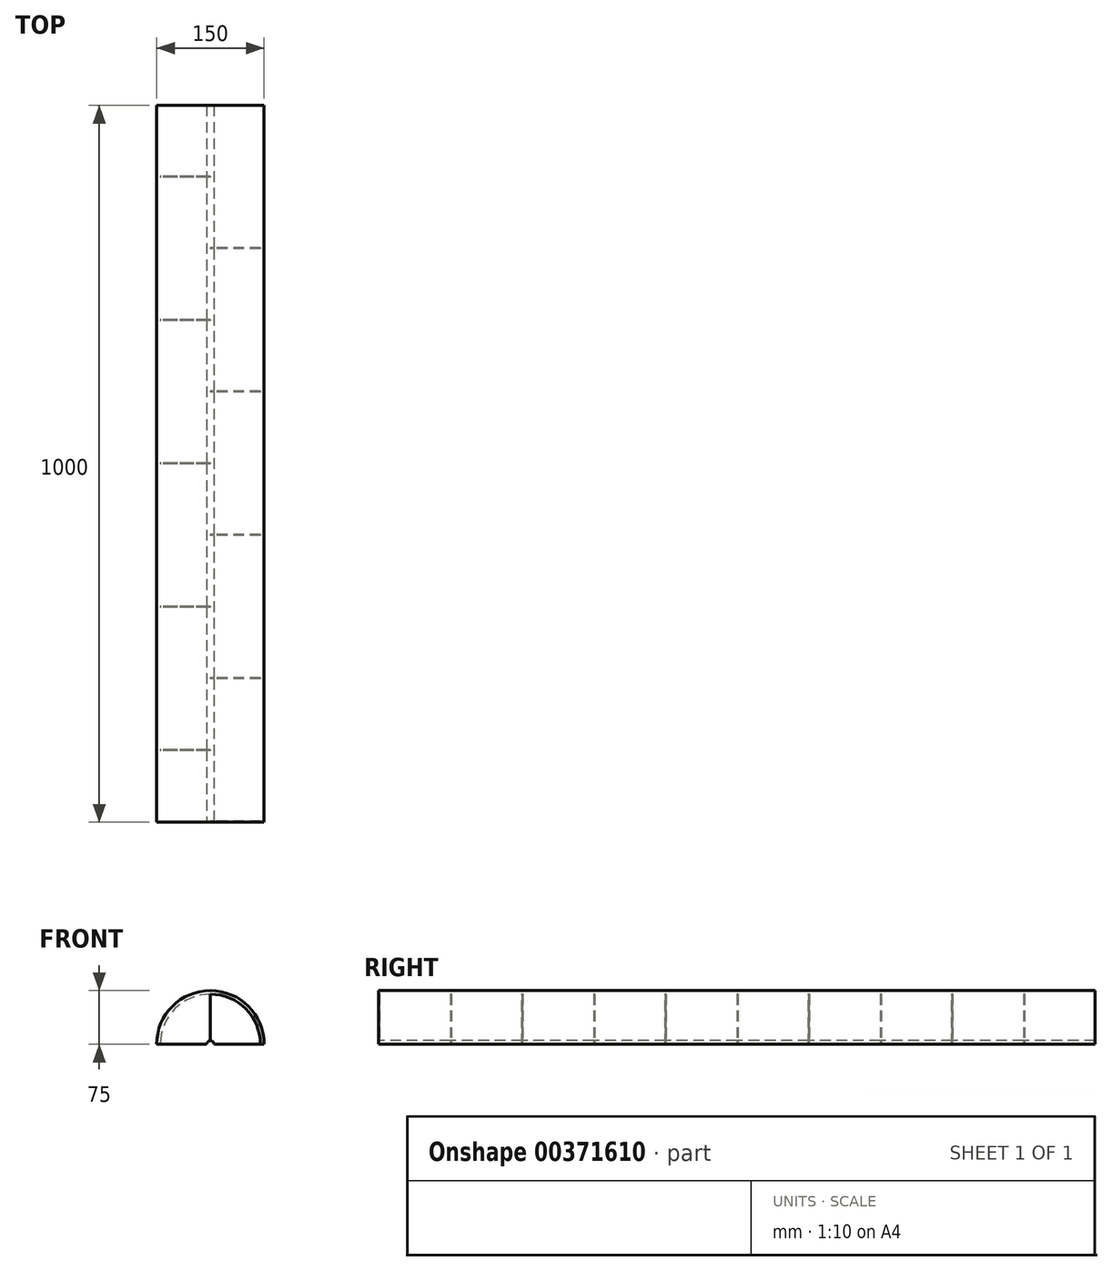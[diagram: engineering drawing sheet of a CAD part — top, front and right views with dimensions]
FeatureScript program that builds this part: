
annotation { "Feature Type Name" : "Feature", "Feature Type Description" : "" }
export const myFeature = defineFeature(function(context is Context, id is Id, definition is map)
    precondition{}
    {
        {
            var Q0;
            Q0=qCreatedBy(makeId("Front.planeOp"),FACE);
            var sketch = newSketch(context, id + "F0", { "sketchPlane" : qUnion([Q0])});
            skCircle(sketch, "E0", {"center": v(0, 0) * mm, "radius": 75 * mm});
            skSolve(sketch);
        }
        {
            var Q0;
            Q0 = qSketchRegion(id + "F0", true);
            extrude(context, id + "F1", {"entities" : qUnion([Q0]), "oppositeDirection" : true, "depth" : 1000 * mm});
        }
        {
            var Q0;
            Q0=qCreatedBy(makeId("Front.planeOp"),FACE);
            var sketch = newSketch(context, id + "F2", { "sketchPlane" : qUnion([Q0])});
            skCircle(sketch, "E1", {"center": v(0, 0) * mm, "radius": 5 * mm});
            skSolve(sketch);
        }
        {
            var Q0;
            Q0 = qSketchRegion(id + "F2", true);
            extrude(context, id + "F3", {"entities" : qUnion([Q0]), "operationType" : NewBodyOperationType.REMOVE, "oppositeDirection" : true, "depth" : 1000 * mm});
        }
        {
            var Q0;
            Q0=qCreatedBy(makeId("Front.planeOp"),FACE);
            var sketch = newSketch(context, id + "F4", { "sketchPlane" : qUnion([Q0])});
            skArc(sketch, "E2", {"start": v(0, -70) * mm, "mid": v(70, 0) * mm, "end": v(0, 70) * mm});
            skLineSegment(sketch, "E3", {"start": v(0, 70) * mm, "end": v(0, -70) * mm});
            skSolve(sketch);
        }
        {
            var Q0;
            Q0 = qSketchRegion(id + "F4", true);
            extrude(context, id + "F5", {"entities" : qUnion([Q0]), "operationType" : NewBodyOperationType.REMOVE, "oppositeDirection" : true, "depth" : 1.2 * mm});
        }
        {
            var Q0;
            Q0=qCreatedBy(makeId("Front.planeOp"),FACE);
            cPlane(context, id + "F6", {"entities" : qUnion([Q0]), "cplaneType" : CPlaneType.OFFSET, "offset" : 100 * mm, "oppositeDirection" : true, "width" : 150 * mm, "height" : 150 * mm});
        }
        {
            var Q0;
            Q0=qCreatedBy(id+"F6.planeOp",FACE);
            var sketch = newSketch(context, id + "F7", { "sketchPlane" : qUnion([Q0])});
            skArc(sketch, "E4", {"start": v(0, 70) * mm, "mid": v(-70, 0) * mm, "end": v(0, -70) * mm});
            skLineSegment(sketch, "E5", {"start": v(0, 70) * mm, "end": v(0, -70) * mm});
            skSolve(sketch);
        }
        {
            var Q0;
            Q0 = qSketchRegion(id + "F7", true);
            extrude(context, id + "F8", {"entities" : qUnion([Q0]), "operationType" : NewBodyOperationType.REMOVE, "oppositeDirection" : true, "depth" : 1.2 * mm});
        }
        {
            var Q0;
            Q0=qCreatedBy(makeId("Front.planeOp"),FACE);
            cPlane(context, id + "F9", {"entities" : qUnion([Q0]), "cplaneType" : CPlaneType.OFFSET, "offset" : 100 * mm, "oppositeDirection" : true, "width" : 150 * mm, "height" : 150 * mm});
        }
        {
            var Q0;
            Q0=qCreatedBy(id+"F9.planeOp",FACE);
            cPlane(context, id + "F10", {"entities" : qUnion([Q0]), "cplaneType" : CPlaneType.OFFSET, "offset" : 100 * mm, "oppositeDirection" : true, "width" : 150 * mm, "height" : 150 * mm});
        }
        {
            var Q0;
            Q0=qCreatedBy(id+"F10.planeOp",FACE);
            cPlane(context, id + "F11", {"entities" : qUnion([Q0]), "cplaneType" : CPlaneType.OFFSET, "offset" : 100 * mm, "oppositeDirection" : true, "width" : 150 * mm, "height" : 150 * mm});
        }
        {
            var Q0;
            Q0=qCreatedBy(id+"F11.planeOp",FACE);
            cPlane(context, id + "F12", {"entities" : qUnion([Q0]), "cplaneType" : CPlaneType.OFFSET, "offset" : 100 * mm, "oppositeDirection" : true, "width" : 150 * mm, "height" : 150 * mm});
        }
        {
            var Q0;
            Q0=qCreatedBy(id+"F12.planeOp",FACE);
            cPlane(context, id + "F13", {"entities" : qUnion([Q0]), "cplaneType" : CPlaneType.OFFSET, "offset" : 100 * mm, "oppositeDirection" : true, "width" : 150 * mm, "height" : 150 * mm});
        }
        {
            var Q0;
            Q0=qCreatedBy(id+"F13.planeOp",FACE);
            cPlane(context, id + "F14", {"entities" : qUnion([Q0]), "cplaneType" : CPlaneType.OFFSET, "offset" : 100 * mm, "oppositeDirection" : true, "width" : 150 * mm, "height" : 150 * mm});
        }
        {
            var Q0;
            Q0=qCreatedBy(id+"F14.planeOp",FACE);
            cPlane(context, id + "F15", {"entities" : qUnion([Q0]), "cplaneType" : CPlaneType.OFFSET, "offset" : 100 * mm, "oppositeDirection" : true, "width" : 150 * mm, "height" : 150 * mm});
        }
        {
            var Q0;
            Q0=qCreatedBy(id+"F15.planeOp",FACE);
            cPlane(context, id + "F16", {"entities" : qUnion([Q0]), "cplaneType" : CPlaneType.OFFSET, "offset" : 100 * mm, "oppositeDirection" : true, "width" : 150 * mm, "height" : 150 * mm});
        }
        {
            var Q0;
            Q0=qCreatedBy(id+"F16.planeOp",FACE);
            cPlane(context, id + "F17", {"entities" : qUnion([Q0]), "cplaneType" : CPlaneType.OFFSET, "offset" : 100 * mm, "oppositeDirection" : true, "width" : 150 * mm, "height" : 150 * mm});
        }
        {
            var Q0;
            Q0=qCreatedBy(id+"F10.planeOp",FACE);
            var sketch = newSketch(context, id + "F18", { "sketchPlane" : qUnion([Q0])});
            skArc(sketch, "E6", {"start": v(0, -70) * mm, "mid": v(70, 0) * mm, "end": v(0, 70) * mm});
            skLineSegment(sketch, "E7", {"start": v(0, 70) * mm, "end": v(0, -70) * mm});
            skSolve(sketch);
        }
        {
            var Q0;
            Q0=qCreatedBy(id+"F11.planeOp",FACE);
            var sketch = newSketch(context, id + "F19", { "sketchPlane" : qUnion([Q0])});
            skArc(sketch, "E8", {"start": v(0, 70) * mm, "mid": v(-70, 0) * mm, "end": v(0, -70) * mm});
            skLineSegment(sketch, "E9", {"start": v(0, 70) * mm, "end": v(0, -70) * mm});
            skSolve(sketch);
        }
        {
            var Q0;
            Q0=qCreatedBy(id+"F12.planeOp",FACE);
            var sketch = newSketch(context, id + "F20", { "sketchPlane" : qUnion([Q0])});
            skArc(sketch, "E10", {"start": v(0, -70) * mm, "mid": v(70, 0) * mm, "end": v(0, 70) * mm});
            skLineSegment(sketch, "E11", {"start": v(0, 70) * mm, "end": v(0, -70) * mm});
            skSolve(sketch);
        }
        {
            var Q0;
            Q0=qCreatedBy(id+"F13.planeOp",FACE);
            var sketch = newSketch(context, id + "F21", { "sketchPlane" : qUnion([Q0])});
            skArc(sketch, "E12", {"start": v(0, 70) * mm, "mid": v(-70, 0) * mm, "end": v(0, -70) * mm});
            skLineSegment(sketch, "E13", {"start": v(0, 70) * mm, "end": v(0, -70) * mm});
            skSolve(sketch);
        }
        {
            var Q0;
            Q0=qCreatedBy(id+"F14.planeOp",FACE);
            var sketch = newSketch(context, id + "F22", { "sketchPlane" : qUnion([Q0])});
            skArc(sketch, "E14", {"start": v(0, -70) * mm, "mid": v(70, 0) * mm, "end": v(0, 70) * mm});
            skLineSegment(sketch, "E15", {"start": v(0, 70) * mm, "end": v(0, -70) * mm});
            skSolve(sketch);
        }
        {
            var Q0;
            Q0=qCreatedBy(id+"F15.planeOp",FACE);
            var sketch = newSketch(context, id + "F23", { "sketchPlane" : qUnion([Q0])});
            skArc(sketch, "E16", {"start": v(0, 70) * mm, "mid": v(-70, 0) * mm, "end": v(0, -70) * mm});
            skLineSegment(sketch, "E17", {"start": v(0, 70) * mm, "end": v(0, -70) * mm});
            skSolve(sketch);
        }
        {
            var Q0;
            Q0=qCreatedBy(id+"F16.planeOp",FACE);
            var sketch = newSketch(context, id + "F24", { "sketchPlane" : qUnion([Q0])});
            skArc(sketch, "E18", {"start": v(0, -70) * mm, "mid": v(70, 0) * mm, "end": v(0, 70) * mm});
            skLineSegment(sketch, "E19", {"start": v(0, 70) * mm, "end": v(0, -70) * mm});
            skSolve(sketch);
        }
        {
            var Q0;
            Q0=qCreatedBy(id+"F17.planeOp",FACE);
            var sketch = newSketch(context, id + "F25", { "sketchPlane" : qUnion([Q0])});
            skArc(sketch, "E20", {"start": v(0, 70) * mm, "mid": v(-70, 0) * mm, "end": v(0, -70) * mm});
            skLineSegment(sketch, "E21", {"start": v(0, 70) * mm, "end": v(0, -70) * mm});
            skSolve(sketch);
        }
        {
            var Q0;
            Q0 = qSketchRegion(id + "F18", true);
            extrude(context, id + "F26", {"entities" : qUnion([Q0]), "operationType" : NewBodyOperationType.REMOVE, "oppositeDirection" : true, "depth" : 1.2 * mm});
        }
        {
            var Q0;
            Q0 = qSketchRegion(id + "F19", true);
            extrude(context, id + "F27", {"entities" : qUnion([Q0]), "operationType" : NewBodyOperationType.REMOVE, "oppositeDirection" : true, "depth" : 1.2 * mm});
        }
        {
            var Q0;
            Q0 = qSketchRegion(id + "F20", true);
            extrude(context, id + "F28", {"entities" : qUnion([Q0]), "operationType" : NewBodyOperationType.REMOVE, "oppositeDirection" : true, "depth" : 1.2 * mm});
        }
        {
            var Q0;
            Q0 = qSketchRegion(id + "F21", true);
            extrude(context, id + "F29", {"entities" : qUnion([Q0]), "operationType" : NewBodyOperationType.REMOVE, "oppositeDirection" : true, "depth" : 1.2 * mm});
        }
        {
            var Q0;
            Q0 = qSketchRegion(id + "F22", true);
            extrude(context, id + "F30", {"entities" : qUnion([Q0]), "operationType" : NewBodyOperationType.REMOVE, "oppositeDirection" : true, "depth" : 1.2 * mm});
        }
        {
            var Q0;
            Q0 = qSketchRegion(id + "F23", true);
            extrude(context, id + "F31", {"entities" : qUnion([Q0]), "operationType" : NewBodyOperationType.REMOVE, "oppositeDirection" : true, "depth" : 1.2 * mm});
        }
        {
            var Q0;
            Q0 = qSketchRegion(id + "F24", true);
            extrude(context, id + "F32", {"entities" : qUnion([Q0]), "operationType" : NewBodyOperationType.REMOVE, "oppositeDirection" : true, "depth" : 1.2 * mm});
        }
        {
            var Q0;
            Q0 = qSketchRegion(id + "F25", true);
            extrude(context, id + "F33", {"entities" : qUnion([Q0]), "operationType" : NewBodyOperationType.REMOVE, "oppositeDirection" : true, "depth" : 1.2 * mm});
        }
        {
            var Q0;
            Q0=qCreatedBy(makeId("Front.planeOp"),FACE);
            var sketch = newSketch(context, id + "F34", { "sketchPlane" : qUnion([Q0])});
            skLineSegment(sketch, "E22.bottom", {"start": v(108.05, -81.9) * mm, "end": v(-110.58, -81.9) * mm});
            skLineSegment(sketch, "E22.top", {"start": v(108.05, 0) * mm, "end": v(-110.58, 0) * mm});
            skLineSegment(sketch, "E22.left", {"start": v(108.05, -81.9) * mm, "end": v(108.05, 0) * mm});
            skLineSegment(sketch, "E22.right", {"start": v(-110.58, -81.9) * mm, "end": v(-110.58, 0) * mm});
            skSolve(sketch);
        }
        {
            var Q0;
            Q0 = qSketchRegion(id + "F34", true);
            extrude(context, id + "F35", {"entities" : qUnion([Q0]), "operationType" : NewBodyOperationType.REMOVE, "oppositeDirection" : true, "depth" : 1000 * mm});
        }
    });
